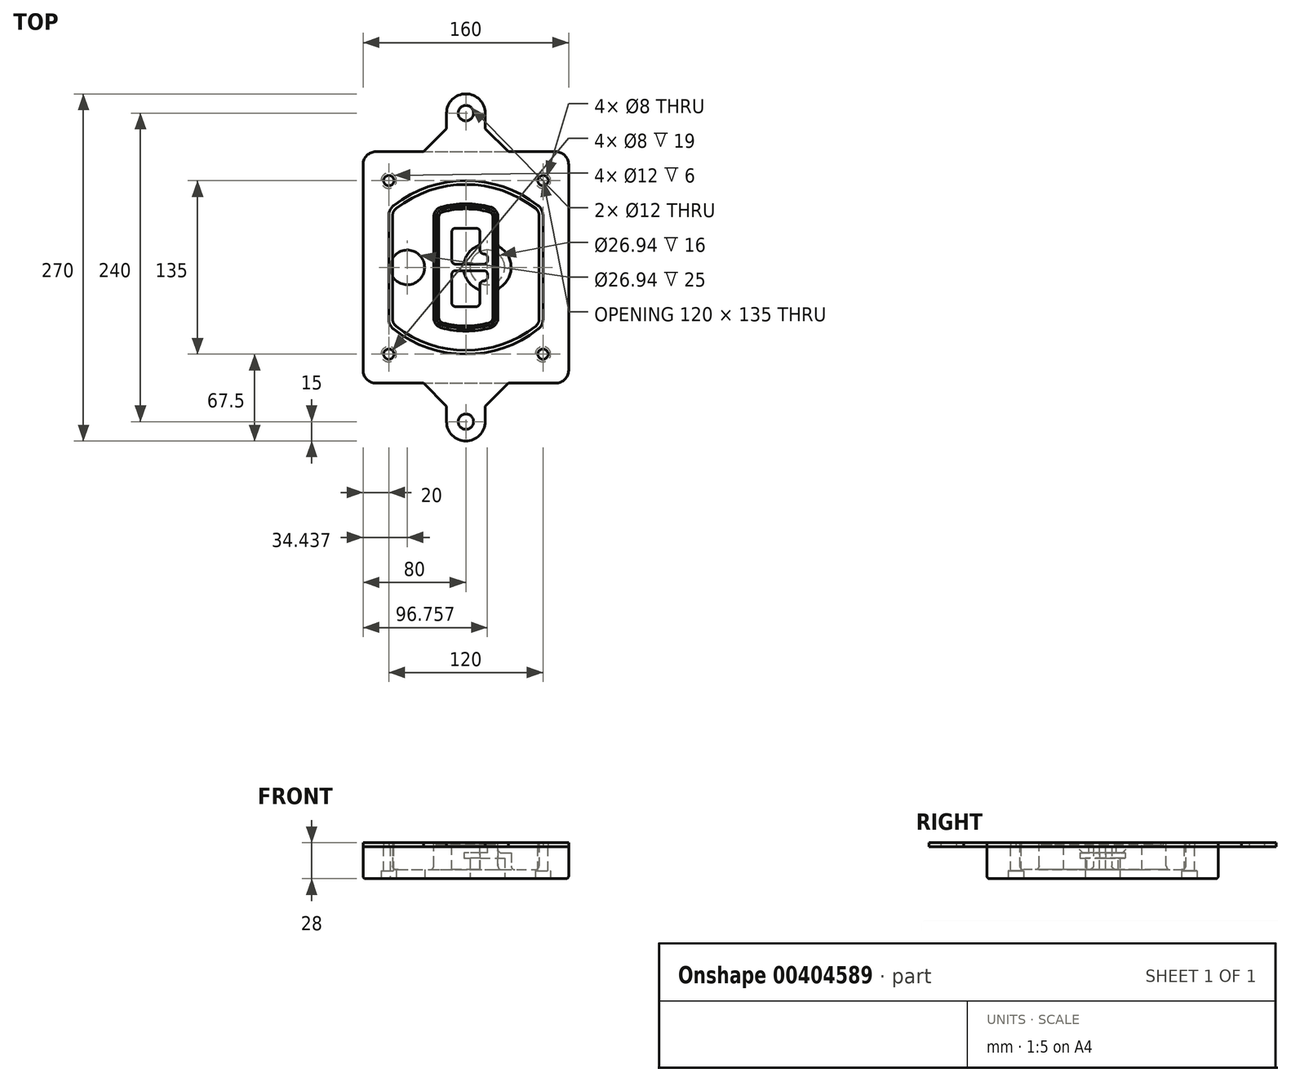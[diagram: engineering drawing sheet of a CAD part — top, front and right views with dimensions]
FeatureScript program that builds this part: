
annotation { "Feature Type Name" : "Feature", "Feature Type Description" : "" }
export const myFeature = defineFeature(function(context is Context, id is Id, definition is map)
    precondition{}
    {
        {
            var Q0;
            Q0=qCreatedBy(makeId("Top.planeOp"),FACE);
            var sketch = newSketch(context, id + "F0", { "sketchPlane" : qUnion([Q0])});
            skPoint(sketch, "E0.rect.middle", {"position": v(0, 0) * mm});
            skLineSegment(sketch, "E1.bottom", {"start": v(-70, -90) * mm, "end": v(70, -90) * mm});
            skLineSegment(sketch, "E1.top", {"start": v(-70, 90) * mm, "end": v(70, 90) * mm});
            skLineSegment(sketch, "E1.left", {"start": v(-80, -80) * mm, "end": v(-80, 80) * mm});
            skLineSegment(sketch, "E1.right", {"start": v(80, -80) * mm, "end": v(80, 80) * mm});
            skLineSegment(sketch, "E2", {"start": v(-80, 90) * mm, "end": v(80, -90) * mm, "construction": true});
            skLineSegment(sketch, "E3", {"start": v(80, 90) * mm, "end": v(-80, -90) * mm, "construction": true});
            skCircle(sketch, "E4", {"center": v(-60, 67.5) * mm, "radius": 4 * mm});
            skCircle(sketch, "E5", {"center": v(60, 67.5) * mm, "radius": 4 * mm});
            skCircle(sketch, "E6", {"center": v(60, -67.5) * mm, "radius": 4 * mm});
            skCircle(sketch, "E7", {"center": v(-60, -67.5) * mm, "radius": 4 * mm});
            skLineSegment(sketch, "E8", {"start": v(-60, 67.5) * mm, "end": v(60, 67.5) * mm, "construction": true});
            skLineSegment(sketch, "E9", {"start": v(60, 67.5) * mm, "end": v(60, -67.5) * mm, "construction": true});
            skLineSegment(sketch, "E10", {"start": v(60, -67.5) * mm, "end": v(-60, -67.5) * mm, "construction": true});
            skLineSegment(sketch, "E11", {"start": v(-60, -67.5) * mm, "end": v(-60, 67.5) * mm, "construction": true});
            skLineSegment(sketch, "E12", {"start": v(-60, 40.3) * mm, "end": v(-60, -40.3) * mm});
            skLineSegment(sketch, "E13", {"start": v(60, 40.3) * mm, "end": v(60, -40.3) * mm});
            skArc(sketch, "E14", {"start": v(56.15, 48.18) * mm, "mid": v(0, 67.5) * mm, "end": v(-56.15, 48.18) * mm});
            skArc(sketch, "E15", {"start": v(-56.15, -48.18) * mm, "mid": v(0, -67.5) * mm, "end": v(56.15, -48.18) * mm});
            skLineSegment(sketch, "E16", {"start": v(-60, 0) * mm, "end": v(60, 0) * mm, "construction": true});
            skPoint(sketch, "E17.visualSharp", {"position": v(-60, -45) * mm});
            skArc(sketch, "E17.filletArc", {"start": v(-60, -40.3) * mm, "mid": v(-58.99, -44.68) * mm, "end": v(-56.15, -48.18) * mm});
            skPoint(sketch, "E18.visualSharp", {"position": v(-60, 45) * mm});
            skArc(sketch, "E18.filletArc", {"start": v(-56.15, 48.18) * mm, "mid": v(-58.99, 44.68) * mm, "end": v(-60, 40.3) * mm});
            skPoint(sketch, "E19.visualSharp", {"position": v(60, 45) * mm});
            skArc(sketch, "E19.filletArc", {"start": v(60, 40.3) * mm, "mid": v(58.99, 44.68) * mm, "end": v(56.15, 48.18) * mm});
            skPoint(sketch, "E20.visualSharp", {"position": v(60, -45) * mm});
            skArc(sketch, "E20.filletArc", {"start": v(56.15, -48.18) * mm, "mid": v(58.99, -44.68) * mm, "end": v(60, -40.3) * mm});
            skPoint(sketch, "E21.visualSharp", {"position": v(-80, 90) * mm});
            skArc(sketch, "E21.filletArc", {"start": v(-70, 90) * mm, "mid": v(-77.07, 87.07) * mm, "end": v(-80, 80) * mm});
            skPoint(sketch, "E22.visualSharp", {"position": v(80, 90) * mm});
            skArc(sketch, "E22.filletArc", {"start": v(80, 80) * mm, "mid": v(77.07, 87.07) * mm, "end": v(70, 90) * mm});
            skPoint(sketch, "E23.visualSharp", {"position": v(80, -90) * mm});
            skArc(sketch, "E23.filletArc", {"start": v(70, -90) * mm, "mid": v(77.07, -87.07) * mm, "end": v(80, -80) * mm});
            skPoint(sketch, "E24.visualSharp", {"position": v(-80, -90) * mm});
            skArc(sketch, "E24.filletArc", {"start": v(-80, -80) * mm, "mid": v(-77.07, -87.07) * mm, "end": v(-70, -90) * mm});
            skArc(sketch, "E25.0", {"start": v(57, 40.3) * mm, "mid": v(56.3, 43.36) * mm, "end": v(54.3, 45.81) * mm});
            skLineSegment(sketch, "E25.1", {"start": v(57, 40.3) * mm, "end": v(57, -40.3) * mm});
            skArc(sketch, "E25.2", {"start": v(54.3, -45.81) * mm, "mid": v(56.3, -43.36) * mm, "end": v(57, -40.3) * mm});
            skArc(sketch, "E25.3", {"start": v(-54.3, -45.81) * mm, "mid": v(0, -64.5) * mm, "end": v(54.3, -45.81) * mm});
            skArc(sketch, "E25.4", {"start": v(-57, -40.3) * mm, "mid": v(-56.3, -43.36) * mm, "end": v(-54.3, -45.81) * mm});
            skArc(sketch, "E25.5", {"start": v(54.3, 45.81) * mm, "mid": v(0, 64.5) * mm, "end": v(-54.3, 45.81) * mm});
            skLineSegment(sketch, "E25.6", {"start": v(-57, 40.3) * mm, "end": v(-57, -40.3) * mm});
            skArc(sketch, "E25.7", {"start": v(-54.3, 45.81) * mm, "mid": v(-56.3, 43.36) * mm, "end": v(-57, 40.3) * mm});
            skArc(sketch, "E26.0", {"start": v(-58.62, 51.33) * mm, "mid": v(-62.58, 46.43) * mm, "end": v(-64, 40.3) * mm});
            skArc(sketch, "E26.1", {"start": v(58.62, 51.33) * mm, "mid": v(0, 71.5) * mm, "end": v(-58.62, 51.33) * mm});
            skArc(sketch, "E26.2", {"start": v(64, 40.3) * mm, "mid": v(62.58, 46.43) * mm, "end": v(58.62, 51.33) * mm});
            skLineSegment(sketch, "E26.3", {"start": v(64, 40.3) * mm, "end": v(64, -40.3) * mm});
            skArc(sketch, "E26.4", {"start": v(58.62, -51.33) * mm, "mid": v(62.58, -46.43) * mm, "end": v(64, -40.3) * mm});
            skLineSegment(sketch, "E26.5", {"start": v(-64, 40.3) * mm, "end": v(-64, -40.3) * mm});
            skArc(sketch, "E26.6", {"start": v(-58.62, -51.33) * mm, "mid": v(0, -71.5) * mm, "end": v(58.62, -51.33) * mm});
            skArc(sketch, "E26.7", {"start": v(-64, -40.3) * mm, "mid": v(-62.58, -46.43) * mm, "end": v(-58.62, -51.33) * mm});
            skSolve(sketch);
        }
        {
            var Q0;
            Q0=makeQuery(id+"F0.imprint","IMPRINT",FACE,{"disambiguationData":[TD([[makeQuery(id+"F0.imprint","IMPRINT",EDGE,{"derivedFrom":sQuery(id+"F0.wireOp",EDGE,"E1.bottom")}),1.0]])]});
            var Q1;
            Q1=makeQuery(id+"F0.imprint","IMPRINT",FACE,{"disambiguationData":[TD([[makeQuery(id+"F0.imprint","IMPRINT",EDGE,{"derivedFrom":sQuery(id+"F0.wireOp",EDGE,"E12")}),1.0]])]});
            var Q2;
            Q2=makeQuery(id+"F0.imprint","IMPRINT",FACE,{"disambiguationData":[TD([[makeQuery(id+"F0.imprint","IMPRINT",EDGE,{"derivedFrom":sQuery(id+"F0.wireOp",EDGE,"E25.0")}),1.0]])]});
            var Q3;
            Q3=makeQuery(id+"F0.imprint","IMPRINT",FACE,{"disambiguationData":[TD([[makeQuery(id+"F0.imprint","IMPRINT",EDGE,{"derivedFrom":sQuery(id+"F0.wireOp",EDGE,"E12")}),-1.0]])]});
            extrude(context, id + "F1", {"entities" : qUnion([Q0, Q1, Q2, Q3]), "oppositeDirection" : true, "depth" : 25 * mm});
        }
        {
            var Q0;
            Q0=makeQuery(id+"F0.imprint","IMPRINT",FACE,{"disambiguationData":[TD([[makeQuery(id+"F0.imprint","IMPRINT",EDGE,{"derivedFrom":sQuery(id+"F0.wireOp",EDGE,"E12")}),1.0]])]});
            extrude(context, id + "F2", {"entities" : qUnion([Q0]), "operationType" : NewBodyOperationType.ADD, "depth" : 3 * mm});
        }
        {
            var Q0;
            Q0=makeQuery(id+"F0.imprint","IMPRINT",FACE,{"disambiguationData":[TD([[makeQuery(id+"F0.imprint","IMPRINT",EDGE,{"derivedFrom":sQuery(id+"F0.wireOp",EDGE,"E25.0")}),1.0]])]});
            extrude(context, id + "F3", {"entities" : qUnion([Q0]), "operationType" : NewBodyOperationType.REMOVE, "oppositeDirection" : true, "depth" : 18 * mm});
        }
        {
            var Q0;
            Q0=makeQuery(id+"F2.opExtrude","CAP_FACE",FACE,{"disambiguationData":[OSD([sQuery(id+"F0.wireOp",EDGE,"E12"),sQuery(id+"F0.wireOp",EDGE,"E13"),sQuery(id+"F0.wireOp",EDGE,"E14"),sQuery(id+"F0.wireOp",EDGE,"E15"),sQuery(id+"F0.wireOp",EDGE,"E17.filletArc"),sQuery(id+"F0.wireOp",EDGE,"E18.filletArc"),sQuery(id+"F0.wireOp",EDGE,"E19.filletArc"),sQuery(id+"F0.wireOp",EDGE,"E20.filletArc"),sQuery(id+"F0.wireOp",EDGE,"E25.0"),sQuery(id+"F0.wireOp",EDGE,"E25.1"),sQuery(id+"F0.wireOp",EDGE,"E25.2"),sQuery(id+"F0.wireOp",EDGE,"E25.3"),sQuery(id+"F0.wireOp",EDGE,"E25.4"),sQuery(id+"F0.wireOp",EDGE,"E25.5"),sQuery(id+"F0.wireOp",EDGE,"E25.6"),sQuery(id+"F0.wireOp",EDGE,"E25.7")])],"isStart":false});
            var sketch = newSketch(context, id + "F4", { "sketchPlane" : qUnion([Q0])});
            skArc(sketch, "E27.0", {"start": v(-19.08, -46.97) * mm, "mid": v(0, -49.5) * mm, "end": v(19.08, -46.97) * mm});
            skArc(sketch, "E28.0", {"start": v(19.08, 46.97) * mm, "mid": v(0, 49.5) * mm, "end": v(-19.08, 46.97) * mm});
            skLineSegment(sketch, "E29", {"start": v(-25, 39.25) * mm, "end": v(-25, -39.25) * mm});
            skLineSegment(sketch, "E30", {"start": v(25, 39.25) * mm, "end": v(25, -39.25) * mm});
            skLineSegment(sketch, "E31", {"start": v(-25, 45.1) * mm, "end": v(25, 45.1) * mm, "construction": true});
            skLineSegment(sketch, "E32", {"start": v(-25, -45.1) * mm, "end": v(25, -45.1) * mm, "construction": true});
            skPoint(sketch, "E33.visualSharp", {"position": v(-25, 45.1) * mm});
            skArc(sketch, "E33.filletArc", {"start": v(-19.08, 46.97) * mm, "mid": v(-23.35, 44.11) * mm, "end": v(-25, 39.25) * mm});
            skPoint(sketch, "E34.visualSharp", {"position": v(25, 45.1) * mm});
            skArc(sketch, "E34.filletArc", {"start": v(25, 39.25) * mm, "mid": v(23.35, 44.11) * mm, "end": v(19.08, 46.97) * mm});
            skPoint(sketch, "E35.visualSharp", {"position": v(25, -45.1) * mm});
            skArc(sketch, "E35.filletArc", {"start": v(19.08, -46.97) * mm, "mid": v(23.35, -44.11) * mm, "end": v(25, -39.25) * mm});
            skPoint(sketch, "E36.visualSharp", {"position": v(-25, -45.1) * mm});
            skArc(sketch, "E36.filletArc", {"start": v(-25, -39.25) * mm, "mid": v(-23.35, -44.11) * mm, "end": v(-19.08, -46.97) * mm});
            skArc(sketch, "E37.0", {"start": v(54.3, 45.81) * mm, "mid": v(0, 64.5) * mm, "end": v(-54.3, 45.81) * mm});
            skArc(sketch, "E37.1", {"start": v(-54.3, 45.81) * mm, "mid": v(-56.3, 43.36) * mm, "end": v(-57, 40.3) * mm});
            skLineSegment(sketch, "E37.2", {"start": v(-57, 40.3) * mm, "end": v(-57, -40.3) * mm});
            skArc(sketch, "E37.3", {"start": v(-57, -40.3) * mm, "mid": v(-56.3, -43.36) * mm, "end": v(-54.3, -45.81) * mm});
            skArc(sketch, "E37.4", {"start": v(-54.3, -45.81) * mm, "mid": v(0, -64.5) * mm, "end": v(54.3, -45.81) * mm});
            skArc(sketch, "E37.5", {"start": v(54.3, -45.81) * mm, "mid": v(56.3, -43.36) * mm, "end": v(57, -40.3) * mm});
            skLineSegment(sketch, "E37.6", {"start": v(57, 40.3) * mm, "end": v(57, -40.3) * mm});
            skArc(sketch, "E37.7", {"start": v(57, 40.3) * mm, "mid": v(56.3, 43.36) * mm, "end": v(54.3, 45.81) * mm});
            skLineSegment(sketch, "E38.0", {"start": v(23, 39.25) * mm, "end": v(23, -39.25) * mm});
            skArc(sketch, "E38.1", {"start": v(18.56, -45.04) * mm, "mid": v(21.76, -42.9) * mm, "end": v(23, -39.25) * mm});
            skArc(sketch, "E38.2", {"start": v(-18.56, -45.04) * mm, "mid": v(0, -47.5) * mm, "end": v(18.56, -45.04) * mm});
            skArc(sketch, "E38.3", {"start": v(-23, -39.25) * mm, "mid": v(-21.76, -42.9) * mm, "end": v(-18.56, -45.04) * mm});
            skLineSegment(sketch, "E38.4", {"start": v(-23, 39.25) * mm, "end": v(-23, -39.25) * mm});
            skArc(sketch, "E38.5", {"start": v(23, 39.25) * mm, "mid": v(21.76, 42.9) * mm, "end": v(18.56, 45.04) * mm});
            skArc(sketch, "E38.6", {"start": v(-18.56, 45.04) * mm, "mid": v(-21.76, 42.9) * mm, "end": v(-23, 39.25) * mm});
            skArc(sketch, "E38.7", {"start": v(18.56, 45.04) * mm, "mid": v(0, 47.5) * mm, "end": v(-18.56, 45.04) * mm});
            skArc(sketch, "E39.0", {"start": v(21, 39.25) * mm, "mid": v(20.18, 41.68) * mm, "end": v(18.04, 43.1) * mm});
            skLineSegment(sketch, "E39.1", {"start": v(21, 39.25) * mm, "end": v(21, -39.25) * mm});
            skArc(sketch, "E39.2", {"start": v(18.04, -43.1) * mm, "mid": v(20.18, -41.68) * mm, "end": v(21, -39.25) * mm});
            skArc(sketch, "E39.3", {"start": v(-18.04, -43.1) * mm, "mid": v(0, -45.5) * mm, "end": v(18.04, -43.1) * mm});
            skArc(sketch, "E39.4", {"start": v(-21, -39.25) * mm, "mid": v(-20.18, -41.68) * mm, "end": v(-18.04, -43.1) * mm});
            skArc(sketch, "E39.5", {"start": v(18.04, 43.1) * mm, "mid": v(0, 45.5) * mm, "end": v(-18.04, 43.1) * mm});
            skLineSegment(sketch, "E39.6", {"start": v(-21, 39.25) * mm, "end": v(-21, -39.25) * mm});
            skArc(sketch, "E39.7", {"start": v(-18.04, 43.1) * mm, "mid": v(-20.18, 41.68) * mm, "end": v(-21, 39.25) * mm});
            skLineSegment(sketch, "E40", {"start": v(-25, 0) * mm, "end": v(25, 0) * mm, "construction": true});
            skLineSegment(sketch, "E41", {"start": v(-11, 5.5) * mm, "end": v(-11, 27.5) * mm});
            skLineSegment(sketch, "E42", {"start": v(-8, 30.5) * mm, "end": v(8, 30.5) * mm});
            skLineSegment(sketch, "E43", {"start": v(11, 27.5) * mm, "end": v(11, 13.5) * mm});
            skLineSegment(sketch, "E44", {"start": v(14, 10.5) * mm, "end": v(14, 10.5) * mm});
            skLineSegment(sketch, "E45", {"start": v(17, 7.5) * mm, "end": v(17, 5.5) * mm});
            skLineSegment(sketch, "E46", {"start": v(14, 2.5) * mm, "end": v(-8, 2.5) * mm});
            skPoint(sketch, "E47.visualSharp", {"position": v(-11, 30.5) * mm});
            skArc(sketch, "E47.filletArc", {"start": v(-8, 30.5) * mm, "mid": v(-10.12, 29.62) * mm, "end": v(-11, 27.5) * mm});
            skPoint(sketch, "E48.visualSharp", {"position": v(11, 30.5) * mm});
            skArc(sketch, "E48.filletArc", {"start": v(11, 27.5) * mm, "mid": v(10.12, 29.62) * mm, "end": v(8, 30.5) * mm});
            skPoint(sketch, "E49.visualSharp", {"position": v(11, 10.5) * mm});
            skArc(sketch, "E49.filletArc", {"start": v(11, 13.5) * mm, "mid": v(11.88, 11.38) * mm, "end": v(14, 10.5) * mm});
            skPoint(sketch, "E50.visualSharp", {"position": v(17, 10.5) * mm});
            skArc(sketch, "E50.filletArc", {"start": v(17, 7.5) * mm, "mid": v(16.12, 9.62) * mm, "end": v(14, 10.5) * mm});
            skPoint(sketch, "E51.visualSharp", {"position": v(17, 2.5) * mm});
            skArc(sketch, "E51.filletArc", {"start": v(14, 2.5) * mm, "mid": v(16.12, 3.38) * mm, "end": v(17, 5.5) * mm});
            skPoint(sketch, "E52.visualSharp", {"position": v(-11, 2.5) * mm});
            skArc(sketch, "E52.filletArc", {"start": v(-11, 5.5) * mm, "mid": v(-10.12, 3.38) * mm, "end": v(-8, 2.5) * mm});
            skLineSegment(sketch, "E53.0.MirrorCS", {"start": v(14, -2.5) * mm, "end": v(-8, -2.5) * mm});
            skArc(sketch, "E54.0.MirrorCS", {"start": v(-11, -5.5) * mm, "mid": v(-10.12, -3.38) * mm, "end": v(-8, -2.5) * mm});
            skLineSegment(sketch, "E55.0.MirrorCS", {"start": v(-11, -5.5) * mm, "end": v(-11, -27.5) * mm});
            skArc(sketch, "E56.0.MirrorCS", {"start": v(-8, -30.5) * mm, "mid": v(-10.12, -29.62) * mm, "end": v(-11, -27.5) * mm});
            skLineSegment(sketch, "E57.0.MirrorCS", {"start": v(-8, -30.5) * mm, "end": v(8, -30.5) * mm});
            skArc(sketch, "E58.0.MirrorCS", {"start": v(11, -27.5) * mm, "mid": v(10.12, -29.62) * mm, "end": v(8, -30.5) * mm});
            skLineSegment(sketch, "E59.0.MirrorCS", {"start": v(11, -27.5) * mm, "end": v(11, -13.5) * mm});
            skArc(sketch, "E60.0.MirrorCS", {"start": v(11, -13.5) * mm, "mid": v(11.88, -11.38) * mm, "end": v(14, -10.5) * mm});
            skArc(sketch, "E61.0.MirrorCS", {"start": v(17, -7.5) * mm, "mid": v(16.12, -9.62) * mm, "end": v(14, -10.5) * mm});
            skLineSegment(sketch, "E62.0.MirrorCS", {"start": v(17, -7.5) * mm, "end": v(17, -5.5) * mm});
            skArc(sketch, "E63.0.MirrorCS", {"start": v(14, -2.5) * mm, "mid": v(16.12, -3.38) * mm, "end": v(17, -5.5) * mm});
            skSolve(sketch);
        }
        {
            var Q0;
            Q0=makeQuery(id+"F4.imprint","IMPRINT",FACE,{"disambiguationData":[TD([[makeQuery(id+"F4.imprint","IMPRINT",EDGE,{"derivedFrom":sQuery(id+"F4.wireOp",EDGE,"E27.0")}),1.0]])]});
            var Q1;
            Q1=makeQuery(id+"F4.imprint","IMPRINT",FACE,{"disambiguationData":[TD([[makeQuery(id+"F4.imprint","IMPRINT",EDGE,{"derivedFrom":sQuery(id+"F4.wireOp",EDGE,"E38.0")}),-1.0]])]});
            var Q2;
            Q2=makeQuery(id+"F4.imprint","IMPRINT",FACE,{"disambiguationData":[TD([[makeQuery(id+"F4.imprint","IMPRINT",EDGE,{"derivedFrom":sQuery(id+"F4.wireOp",EDGE,"E39.0")}),1.0]])]});
            extrude(context, id + "F5", {"entities" : qUnion([Q0, Q1, Q2]), "operationType" : NewBodyOperationType.ADD, "endBound" : BoundingType.UP_TO_NEXT, "oppositeDirection" : true, "depth" : 25 * mm});
        }
        {
            var Q0;
            Q0=makeQuery(id+"F4.imprint","IMPRINT",FACE,{"disambiguationData":[TD([[makeQuery(id+"F4.imprint","IMPRINT",EDGE,{"derivedFrom":sQuery(id+"F4.wireOp",EDGE,"E38.0")}),-1.0]])]});
            extrude(context, id + "F6", {"entities" : qUnion([Q0]), "operationType" : NewBodyOperationType.REMOVE, "oppositeDirection" : true, "depth" : 2 * mm});
        }
        {
            var Q0;
            Q0=makeQuery(id+"F1.opExtrude","CAP_FACE",FACE,{"disambiguationData":[OSD([sQuery(id+"F0.wireOp",EDGE,"E1.bottom"),sQuery(id+"F0.wireOp",EDGE,"E1.top"),sQuery(id+"F0.wireOp",EDGE,"E1.left"),sQuery(id+"F0.wireOp",EDGE,"E1.right"),sQuery(id+"F0.wireOp",EDGE,"E4"),sQuery(id+"F0.wireOp",EDGE,"E5"),sQuery(id+"F0.wireOp",EDGE,"E6"),sQuery(id+"F0.wireOp",EDGE,"E7"),sQuery(id+"F0.wireOp",EDGE,"E21.filletArc"),sQuery(id+"F0.wireOp",EDGE,"E22.filletArc"),sQuery(id+"F0.wireOp",EDGE,"E23.filletArc"),sQuery(id+"F0.wireOp",EDGE,"E24.filletArc")])],"isStart":false});
            var sketch = newSketch(context, id + "F7", { "sketchPlane" : qUnion([Q0])});
            skCircle(sketch, "E64", {"center": v(16.76, 0) * mm, "radius": 13.47 * mm});
            skCircle(sketch, "E65", {"center": v(-45.56, 0) * mm, "radius": 13.47 * mm});
            skLineSegment(sketch, "E66", {"start": v(80, 0) * mm, "end": v(-80, 0) * mm});
            skCircle(sketch, "E67", {"center": v(16.76, 0) * mm, "radius": 18.47 * mm});
            skCircle(sketch, "E68", {"center": v(60, -67.5) * mm, "radius": 6 * mm});
            skCircle(sketch, "E69", {"center": v(-60, -67.5) * mm, "radius": 6 * mm});
            skCircle(sketch, "E70", {"center": v(-60, 67.5) * mm, "radius": 6 * mm});
            skCircle(sketch, "E71", {"center": v(60, 67.5) * mm, "radius": 6 * mm});
            skSolve(sketch);
        }
        {
            var Q0;
            {var subQ1=sQuery(id+"F7.wireOp",EDGE,"E66");var subQ4=sQuery(id+"F7.wireOp",EDGE,"E64");var subQ6=makeQuery(id+"F7.imprint","INTERSECT",VERTEX,{"disambiguationData":[OD(0.0)],"derivedFrom":[subQ4,subQ1]});Q0=makeQuery(id+"F7.imprint","IMPRINT",FACE,{"disambiguationData":[TD([[makeQuery(id+"F7.imprint","IMPRINT",EDGE,{"disambiguationData":[TD([[subQ6,-1.0]])],"derivedFrom":subQ4}),-1.0]])]});}
            var Q1;
            {var subQ0=sQuery(id+"F7.wireOp",EDGE,"E66");var subQ1=sQuery(id+"F7.wireOp",EDGE,"E64");var subQ3=makeQuery(id+"F7.imprint","INTERSECT",VERTEX,{"disambiguationData":[OD(0.0)],"derivedFrom":[subQ1,subQ0]});Q1=makeQuery(id+"F7.imprint","IMPRINT",FACE,{"disambiguationData":[TD([[makeQuery(id+"F7.imprint","IMPRINT",EDGE,{"disambiguationData":[TD([[subQ3,-1.0]])],"derivedFrom":subQ1}),1.0]])]});}
            var Q2;
            {var subQ0=sQuery(id+"F7.wireOp",EDGE,"E66");var subQ1=sQuery(id+"F7.wireOp",EDGE,"E64");var subQ3=makeQuery(id+"F7.imprint","INTERSECT",VERTEX,{"disambiguationData":[OD(0.0)],"derivedFrom":[subQ1,subQ0]});Q2=makeQuery(id+"F7.imprint","IMPRINT",FACE,{"disambiguationData":[TD([[makeQuery(id+"F7.imprint","IMPRINT",EDGE,{"disambiguationData":[TD([[subQ3,1.0]])],"derivedFrom":subQ1}),1.0]])]});}
            var Q3;
            {var subQ1=sQuery(id+"F7.wireOp",EDGE,"E66");var subQ4=sQuery(id+"F7.wireOp",EDGE,"E64");var subQ6=makeQuery(id+"F7.imprint","INTERSECT",VERTEX,{"disambiguationData":[OD(0.0)],"derivedFrom":[subQ4,subQ1]});Q3=makeQuery(id+"F7.imprint","IMPRINT",FACE,{"disambiguationData":[TD([[makeQuery(id+"F7.imprint","IMPRINT",EDGE,{"disambiguationData":[TD([[subQ6,1.0]])],"derivedFrom":subQ4}),-1.0]])]});}
            extrude(context, id + "F8", {"entities" : qUnion([Q0, Q1, Q2, Q3]), "operationType" : NewBodyOperationType.ADD, "oppositeDirection" : true, "depth" : 20 * mm});
        }
        {
            var Q0;
            {var subQ0=sQuery(id+"F7.wireOp",EDGE,"E66");var subQ1=sQuery(id+"F7.wireOp",EDGE,"E64");var subQ3=makeQuery(id+"F7.imprint","INTERSECT",VERTEX,{"disambiguationData":[OD(0.0)],"derivedFrom":[subQ1,subQ0]});Q0=makeQuery(id+"F7.imprint","IMPRINT",FACE,{"disambiguationData":[TD([[makeQuery(id+"F7.imprint","IMPRINT",EDGE,{"disambiguationData":[TD([[subQ3,-1.0]])],"derivedFrom":subQ1}),1.0]])]});}
            var Q1;
            {var subQ0=sQuery(id+"F7.wireOp",EDGE,"E66");var subQ1=sQuery(id+"F7.wireOp",EDGE,"E64");var subQ3=makeQuery(id+"F7.imprint","INTERSECT",VERTEX,{"disambiguationData":[OD(0.0)],"derivedFrom":[subQ1,subQ0]});Q1=makeQuery(id+"F7.imprint","IMPRINT",FACE,{"disambiguationData":[TD([[makeQuery(id+"F7.imprint","IMPRINT",EDGE,{"disambiguationData":[TD([[subQ3,1.0]])],"derivedFrom":subQ1}),1.0]])]});}
            extrude(context, id + "F9", {"entities" : qUnion([Q0, Q1]), "operationType" : NewBodyOperationType.REMOVE, "oppositeDirection" : true, "depth" : 16 * mm});
        }
        {
            var Q0;
            {var subQ0=sQuery(id+"F7.wireOp",EDGE,"E66");var subQ1=sQuery(id+"F7.wireOp",EDGE,"E65");var subQ3=makeQuery(id+"F7.imprint","INTERSECT",VERTEX,{"disambiguationData":[OD(0.0)],"derivedFrom":[subQ1,subQ0]});Q0=makeQuery(id+"F7.imprint","IMPRINT",FACE,{"disambiguationData":[TD([[makeQuery(id+"F7.imprint","IMPRINT",EDGE,{"disambiguationData":[TD([[subQ3,-1.0]])],"derivedFrom":subQ1}),1.0]])]});}
            var Q1;
            {var subQ0=sQuery(id+"F7.wireOp",EDGE,"E66");var subQ1=sQuery(id+"F7.wireOp",EDGE,"E65");var subQ3=makeQuery(id+"F7.imprint","INTERSECT",VERTEX,{"disambiguationData":[OD(0.0)],"derivedFrom":[subQ1,subQ0]});Q1=makeQuery(id+"F7.imprint","IMPRINT",FACE,{"disambiguationData":[TD([[makeQuery(id+"F7.imprint","IMPRINT",EDGE,{"disambiguationData":[TD([[subQ3,1.0]])],"derivedFrom":subQ1}),1.0]])]});}
            extrude(context, id + "F10", {"entities" : qUnion([Q0, Q1]), "operationType" : NewBodyOperationType.REMOVE, "oppositeDirection" : true, "depth" : 25 * mm});
        }
        {
            var Q0;
            Q0=makeQuery(id+"F7.imprint","IMPRINT",FACE,{"disambiguationData":[TD([[makeQuery(id+"F7.imprint","IMPRINT",EDGE,{"derivedFrom":sQuery(id+"F7.wireOp",EDGE,"E68")}),1.0]])]});
            var Q1;
            Q1=makeQuery(id+"F7.imprint","IMPRINT",FACE,{"disambiguationData":[TD([[makeQuery(id+"F7.imprint","IMPRINT",EDGE,{"derivedFrom":makeQuery(id+"F1.opExtrude","CAP_EDGE",EDGE,{"disambiguationData":[OSD([sQuery(id+"F0.wireOp",EDGE,"E5")])],"isStart":false})}),-1.0]])]});
            var Q2;
            Q2=makeQuery(id+"F7.imprint","IMPRINT",FACE,{"disambiguationData":[TD([[makeQuery(id+"F7.imprint","IMPRINT",EDGE,{"derivedFrom":sQuery(id+"F7.wireOp",EDGE,"E69")}),1.0]])]});
            var Q3;
            Q3=makeQuery(id+"F7.imprint","IMPRINT",FACE,{"disambiguationData":[TD([[makeQuery(id+"F7.imprint","IMPRINT",EDGE,{"derivedFrom":makeQuery(id+"F1.opExtrude","CAP_EDGE",EDGE,{"disambiguationData":[OSD([sQuery(id+"F0.wireOp",EDGE,"E4")])],"isStart":false})}),-1.0]])]});
            var Q4;
            Q4=makeQuery(id+"F7.imprint","IMPRINT",FACE,{"disambiguationData":[TD([[makeQuery(id+"F7.imprint","IMPRINT",EDGE,{"derivedFrom":sQuery(id+"F7.wireOp",EDGE,"E70")}),1.0]])]});
            var Q5;
            Q5=makeQuery(id+"F7.imprint","IMPRINT",FACE,{"disambiguationData":[TD([[makeQuery(id+"F7.imprint","IMPRINT",EDGE,{"derivedFrom":makeQuery(id+"F1.opExtrude","CAP_EDGE",EDGE,{"disambiguationData":[OSD([sQuery(id+"F0.wireOp",EDGE,"E7")])],"isStart":false})}),-1.0]])]});
            var Q6;
            Q6=makeQuery(id+"F7.imprint","IMPRINT",FACE,{"disambiguationData":[TD([[makeQuery(id+"F7.imprint","IMPRINT",EDGE,{"derivedFrom":sQuery(id+"F7.wireOp",EDGE,"E71")}),1.0]])]});
            var Q7;
            Q7=makeQuery(id+"F7.imprint","IMPRINT",FACE,{"disambiguationData":[TD([[makeQuery(id+"F7.imprint","IMPRINT",EDGE,{"derivedFrom":makeQuery(id+"F1.opExtrude","CAP_EDGE",EDGE,{"disambiguationData":[OSD([sQuery(id+"F0.wireOp",EDGE,"E6")])],"isStart":false})}),-1.0]])]});
            extrude(context, id + "F11", {"entities" : qUnion([Q0, Q1, Q2, Q3, Q4, Q5, Q6, Q7]), "operationType" : NewBodyOperationType.REMOVE, "oppositeDirection" : true, "depth" : 6 * mm});
        }
        {
            var Q0;
            Q0=makeQuery(id+"F9.boolean.opBoolean","COPY",FACE,{"derivedFrom":makeQuery(id+"F9.opExtrude","CAP_FACE",FACE,{"disambiguationData":[OSD([sQuery(id+"F7.wireOp",EDGE,"E64")])],"isStart":false})});
            var sketch = newSketch(context, id + "F12", { "sketchPlane" : qUnion([Q0])});
            skArc(sketch, "E72.0", {"start": v(11, 17.55) * mm, "mid": v(2.57, 11.82) * mm, "end": v(-1.54, 2.5) * mm});
            skArc(sketch, "E72.1", {"start": v(-1.54, -2.5) * mm, "mid": v(2.57, -11.82) * mm, "end": v(11, -17.55) * mm});
            skLineSegment(sketch, "E73", {"start": v(-1.54, -2.5) * mm, "end": v(14, -2.5) * mm});
            skLineSegment(sketch, "E74.0", {"start": v(14, 2.5) * mm, "end": v(-1.54, 2.5) * mm});
            skArc(sketch, "E74.1", {"start": v(14, 2.5) * mm, "mid": v(16.12, 3.38) * mm, "end": v(17, 5.5) * mm});
            skLineSegment(sketch, "E74.2", {"start": v(17, 7.5) * mm, "end": v(17, 5.5) * mm});
            skArc(sketch, "E74.3", {"start": v(17, 7.5) * mm, "mid": v(16.12, 9.62) * mm, "end": v(14, 10.5) * mm});
            skArc(sketch, "E74.4", {"start": v(11, 13.5) * mm, "mid": v(11.88, 11.38) * mm, "end": v(14, 10.5) * mm});
            skLineSegment(sketch, "E74.5", {"start": v(11, 17.55) * mm, "end": v(11, 13.5) * mm});
            skLineSegment(sketch, "E74.7", {"start": v(14, -2.5) * mm, "end": v(-1.54, -2.5) * mm});
            skArc(sketch, "E74.8", {"start": v(14, -2.5) * mm, "mid": v(16.12, -3.38) * mm, "end": v(17, -5.5) * mm});
            skLineSegment(sketch, "E74.9", {"start": v(17, -7.5) * mm, "end": v(17, -5.5) * mm});
            skArc(sketch, "E74.10", {"start": v(17, -7.5) * mm, "mid": v(16.12, -9.62) * mm, "end": v(14, -10.5) * mm});
            skArc(sketch, "E74.11", {"start": v(11, -13.5) * mm, "mid": v(11.88, -11.38) * mm, "end": v(14, -10.5) * mm});
            skLineSegment(sketch, "E74.12", {"start": v(11, -17.55) * mm, "end": v(11, -13.5) * mm});
            skPoint(sketch, "E75.orphan", {"position": v(11, -27.5) * mm});
            skPoint(sketch, "E76.orphan", {"position": v(-8, -2.5) * mm});
            skPoint(sketch, "E77.orphan", {"position": v(-8, 2.5) * mm});
            skPoint(sketch, "E78.orphan", {"position": v(11, 27.5) * mm});
            skSolve(sketch);
        }
        {
            var Q0;
            {var subQ7=sQuery(id+"F12.wireOp",EDGE,"E72.0");var subQ14=sQuery(id+"F12.wireOp",EDGE,"E72.1");var subQ16=sQuery(id+"F12.wireOp",EDGE,"E74.1");var subQ18=sQuery(id+"F12.wireOp",EDGE,"E74.8");Q0=qUnion([makeQuery(id+"F12.imprint","IMPRINT",FACE,{"disambiguationData":[TD([[makeQuery(id+"F12.imprint","IMPRINT",EDGE,{"derivedFrom":subQ7}),1.0]])]}),makeQuery(id+"F12.imprint","IMPRINT",FACE,{"disambiguationData":[TD([[makeQuery(id+"F12.imprint","IMPRINT",EDGE,{"derivedFrom":subQ14}),1.0]])]}),makeQuery(id+"F12.imprint","IMPRINT",FACE,{"disambiguationData":[TD([[makeQuery(id+"F12.imprint","IMPRINT",EDGE,{"derivedFrom":subQ16}),1.0]])]}),makeQuery(id+"F12.imprint","IMPRINT",FACE,{"disambiguationData":[TD([[makeQuery(id+"F12.imprint","IMPRINT",EDGE,{"derivedFrom":subQ18}),-1.0]])]})]);}
            var Q1;
            Q1=makeQuery(id+"F5.boolean.opBoolean","SPLIT",FACE,{"disambiguationData":[TD([makeQuery(id+"F5.opExtrude","SWEPT_FACE",FACE,{"disambiguationData":[OSD([sQuery(id+"F4.wireOp",EDGE,"E41")])]})])],"derivedFrom":makeQuery(id+"F3.boolean.opBoolean","COPY",FACE,{"derivedFrom":makeQuery(id+"F3.opExtrude","CAP_FACE",FACE,{"disambiguationData":[OSD([sQuery(id+"F0.wireOp",EDGE,"E25.0"),sQuery(id+"F0.wireOp",EDGE,"E25.1"),sQuery(id+"F0.wireOp",EDGE,"E25.2"),sQuery(id+"F0.wireOp",EDGE,"E25.3"),sQuery(id+"F0.wireOp",EDGE,"E25.4"),sQuery(id+"F0.wireOp",EDGE,"E25.5"),sQuery(id+"F0.wireOp",EDGE,"E25.6"),sQuery(id+"F0.wireOp",EDGE,"E25.7")])],"isStart":false})})});
            extrude(context, id + "F13", {"entities" : qUnion([Q0]), "operationType" : NewBodyOperationType.REMOVE, "endBound" : BoundingType.UP_TO_SURFACE, "endBoundEntityFace" : qUnion([Q1]), "depth" : 25 * mm});
        }
        {
            var Q0;
            Q0=makeQuery(id+"F3.boolean.opBoolean","COPY",EDGE,{"derivedFrom":makeQuery(id+"F3.opExtrude","CAP_EDGE",EDGE,{"disambiguationData":[OSD([sQuery(id+"F0.wireOp",EDGE,"E25.6")])],"isStart":false})});
            var Q1;
            Q1=makeQuery(id+"F8.boolean.opBoolean","INTERSECT",EDGE,{"derivedFrom":[makeQuery(id+"F5.opExtrude","SWEPT_FACE",FACE,{"disambiguationData":[OSD([sQuery(id+"F4.wireOp",EDGE,"E30")])]}),makeQuery(id+"F8.opExtrude","CAP_FACE",FACE,{"disambiguationData":[OSD([sQuery(id+"F7.wireOp",EDGE,"E67")])],"isStart":false})]});
            var Q2;
            Q2=makeQuery(id+"F8.boolean.opBoolean","INTERSECT",EDGE,{"disambiguationData":[OD(1.0)],"derivedFrom":[makeQuery(id+"F5.opExtrude","SWEPT_FACE",FACE,{"disambiguationData":[OSD([sQuery(id+"F4.wireOp",EDGE,"E30")])]}),makeQuery(id+"F8.opExtrude","SWEPT_FACE",FACE,{"disambiguationData":[OSD([sQuery(id+"F7.wireOp",EDGE,"E67")])]})]});
            var Q3;
            {var subQ0=sQuery(id+"F4.wireOp",EDGE,"E30");Q3=makeQuery(id+"F8.boolean.opBoolean","SPLIT",EDGE,{"disambiguationData":[TD([makeQuery(id+"F5.opExtrude","SWEPT_FACE",FACE,{"disambiguationData":[OSD([sQuery(id+"F4.wireOp",EDGE,"E35.filletArc")])]})])],"derivedFrom":makeQuery(id+"F5.opExtrude","CAP_EDGE",EDGE,{"disambiguationData":[OSD([subQ0])],"isStart":false})});}
            var Q4;
            {var subQ0=sQuery(id+"F0.wireOp",EDGE,"E25.7");var subQ1=sQuery(id+"F0.wireOp",EDGE,"E25.1");var subQ2=sQuery(id+"F0.wireOp",EDGE,"E25.6");var subQ3=sQuery(id+"F0.wireOp",EDGE,"E25.5");var subQ4=sQuery(id+"F0.wireOp",EDGE,"E25.4");var subQ5=sQuery(id+"F0.wireOp",EDGE,"E25.0");var subQ6=sQuery(id+"F0.wireOp",EDGE,"E25.2");var subQ7=sQuery(id+"F0.wireOp",EDGE,"E25.3");Q4=makeQuery(id+"F8.boolean.opBoolean","INTERSECT",EDGE,{"derivedFrom":[makeQuery(id+"F5.boolean.opBoolean","SPLIT",FACE,{"disambiguationData":[TD([makeQuery(id+"F2.opExtrude","SWEPT_FACE",FACE,{"disambiguationData":[OSD([subQ5])]})])],"derivedFrom":makeQuery(id+"F3.boolean.opBoolean","COPY",FACE,{"derivedFrom":makeQuery(id+"F3.opExtrude","CAP_FACE",FACE,{"disambiguationData":[OSD([subQ5,subQ1,subQ6,subQ7,subQ4,subQ3,subQ2,subQ0])],"isStart":false})})}),makeQuery(id+"F8.opExtrude","SWEPT_FACE",FACE,{"disambiguationData":[OSD([sQuery(id+"F7.wireOp",EDGE,"E67")])]})]});}
            var Q5;
            Q5=makeQuery(id+"F8.boolean.opBoolean","INTERSECT",EDGE,{"disambiguationData":[OD(0.0)],"derivedFrom":[makeQuery(id+"F5.opExtrude","SWEPT_FACE",FACE,{"disambiguationData":[OSD([sQuery(id+"F4.wireOp",EDGE,"E30")])]}),makeQuery(id+"F8.opExtrude","SWEPT_FACE",FACE,{"disambiguationData":[OSD([sQuery(id+"F7.wireOp",EDGE,"E67")])]})]});
            fillet(context, id + "F14", {"entities" : qUnion([Q0, Q1, Q2, Q3, Q4, Q5]), "radius" : 3 * mm, "tangentPropagation" : true, "allowEdgeOverflow" : false});
        }
        {
            var Q0;
            Q0=makeQuery(id+"F1.opExtrude","CAP_EDGE",EDGE,{"disambiguationData":[OSD([sQuery(id+"F0.wireOp",EDGE,"E1.bottom")])],"isStart":false});
            fillet(context, id + "F15", {"entities" : qUnion([Q0]), "radius" : 2 * mm, "tangentPropagation" : true, "allowEdgeOverflow" : false});
        }
        {
            var Q0;
            {var subQ0=sQuery(id+"F0.wireOp",EDGE,"E21.filletArc");var subQ1=sQuery(id+"F0.wireOp",EDGE,"E7");var subQ2=sQuery(id+"F0.wireOp",EDGE,"E6");var subQ3=sQuery(id+"F0.wireOp",EDGE,"E5");var subQ4=sQuery(id+"F0.wireOp",EDGE,"E4");var subQ5=sQuery(id+"F0.wireOp",EDGE,"E22.filletArc");var subQ6=sQuery(id+"F0.wireOp",EDGE,"E1.bottom");var subQ7=sQuery(id+"F0.wireOp",EDGE,"E1.right");var subQ8=sQuery(id+"F0.wireOp",EDGE,"E1.top");var subQ9=sQuery(id+"F0.wireOp",EDGE,"E1.left");var subQ10=sQuery(id+"F0.wireOp",EDGE,"E23.filletArc");var subQ11=sQuery(id+"F0.wireOp",EDGE,"E24.filletArc");Q0=makeQuery(id+"F2.boolean.opBoolean","SPLIT",FACE,{"disambiguationData":[TD([makeQuery(id+"F1.opExtrude","SWEPT_FACE",FACE,{"disambiguationData":[OSD([subQ6])]})])],"derivedFrom":makeQuery(id+"F1.opExtrude","CAP_FACE",FACE,{"disambiguationData":[OSD([subQ6,subQ8,subQ9,subQ7,subQ4,subQ3,subQ2,subQ1,subQ0,subQ5,subQ10,subQ11])],"isStart":true})});}
            var sketch = newSketch(context, id + "F16", { "sketchPlane" : qUnion([Q0])});
            skLineSegment(sketch, "E79", {"start": v(-33, 90) * mm, "end": v(-15, 108) * mm});
            skLineSegment(sketch, "E80", {"start": v(-15, 108) * mm, "end": v(-15, 120) * mm});
            skLineSegment(sketch, "E81", {"start": v(15, 120) * mm, "end": v(15, 108) * mm});
            skLineSegment(sketch, "E82", {"start": v(15, 108) * mm, "end": v(33, 90) * mm});
            skArc(sketch, "E83", {"start": v(15, 120) * mm, "mid": v(0, 135) * mm, "end": v(-15, 120) * mm});
            skCircle(sketch, "E84", {"center": v(0, 120) * mm, "radius": 6 * mm});
            skLineSegment(sketch, "E85", {"start": v(0, 120) * mm, "end": v(0, 90) * mm, "construction": true});
            skLineSegment(sketch, "E86", {"start": v(-80, 0) * mm, "end": v(80, 0) * mm, "construction": true});
            skLineSegment(sketch, "E87.MirrorCS", {"start": v(-15, -108) * mm, "end": v(-15, -120) * mm});
            skLineSegment(sketch, "E88.MirrorCS", {"start": v(15, -120) * mm, "end": v(15, -108) * mm});
            skLineSegment(sketch, "E89.MirrorCS", {"start": v(-33, -90) * mm, "end": v(-15, -108) * mm});
            skLineSegment(sketch, "E90.MirrorCS", {"start": v(15, -108) * mm, "end": v(33, -90) * mm});
            skArc(sketch, "E91.MirrorCS", {"start": v(15, -120) * mm, "mid": v(0, -135) * mm, "end": v(-15, -120) * mm});
            skLineSegment(sketch, "E92.MirrorCS", {"start": v(0, -120) * mm, "end": v(0, -90) * mm, "construction": true});
            skCircle(sketch, "E93.MirrorC", {"center": v(0, -120) * mm, "radius": 6 * mm});
            skSolve(sketch);
        }
        {
            var Q0;
            {var subQ1=sQuery(id+"F16.wireOp",EDGE,"E79");Q0=makeQuery(id+"F16.imprint","IMPRINT",FACE,{"disambiguationData":[TD([[makeQuery(id+"F16.imprint","IMPRINT",EDGE,{"derivedFrom":subQ1}),-1.0]])]});}
            var Q1;
            Q1=makeQuery(id+"F16.imprint","IMPRINT",FACE,{"disambiguationData":[TD([[makeQuery(id+"F16.imprint","IMPRINT",EDGE,{"derivedFrom":sQuery(id+"F16.wireOp",EDGE,"E87.MirrorCS")}),1.0]])]});
            var Q2;
            Q2=makeQuery(id+"F16.imprint","IMPRINT",FACE,{"disambiguationData":[TD([[makeQuery(id+"F16.imprint","IMPRINT",EDGE,{"derivedFrom":makeQuery(id+"F1.opExtrude","CAP_EDGE",EDGE,{"disambiguationData":[OSD([sQuery(id+"F0.wireOp",EDGE,"E1.left")])],"isStart":true})}),-1.0]])]});
            extrude(context, id + "F17", {"entities" : qUnion([Q0, Q1, Q2]), "depth" : 3 * mm});
        }
    });
